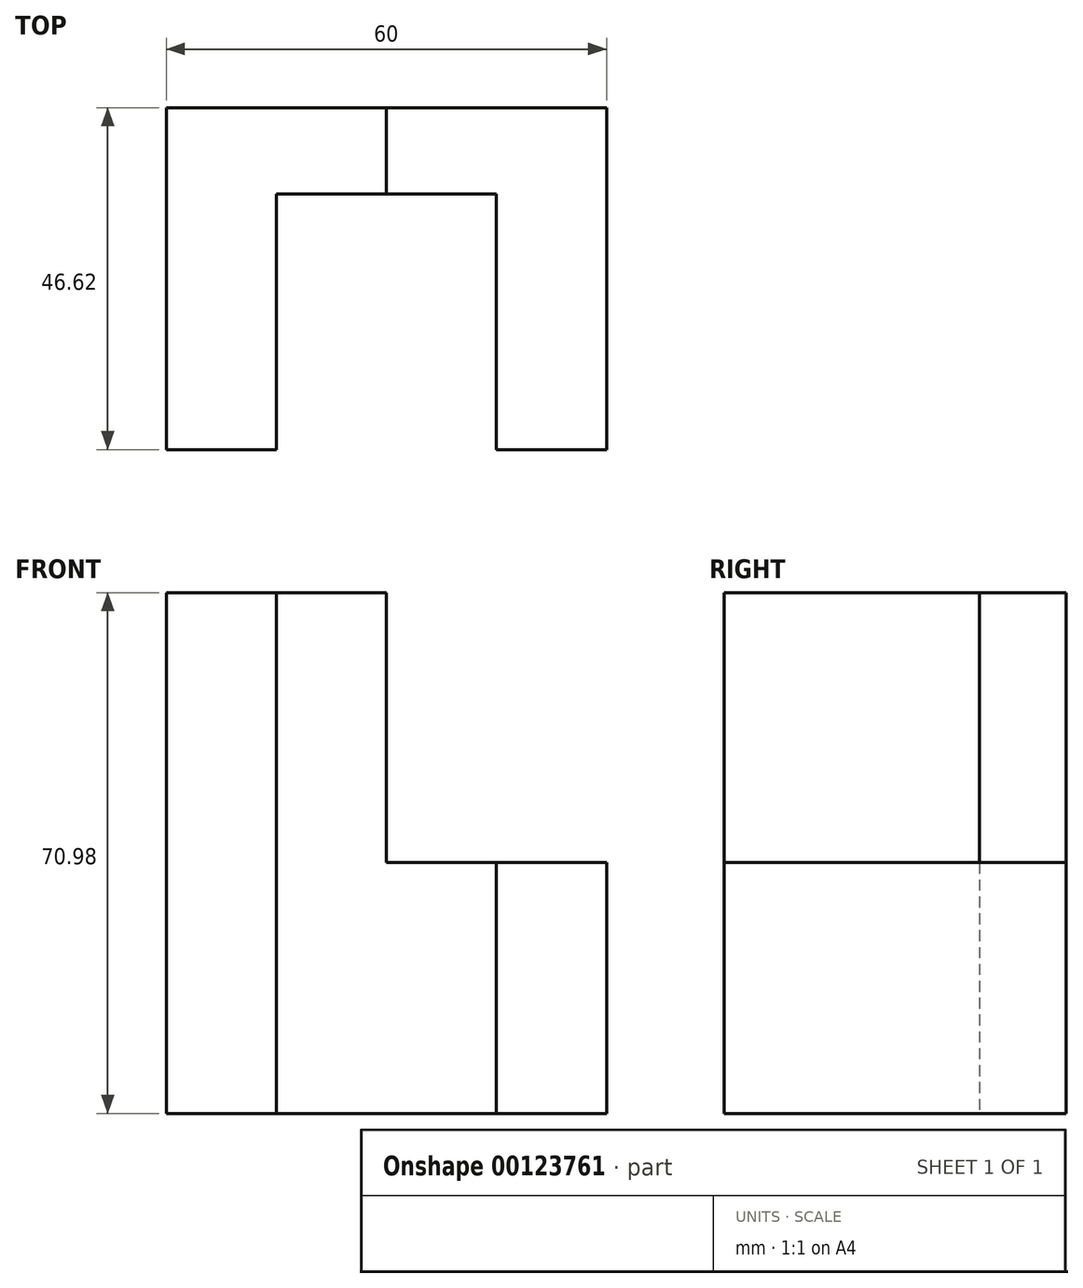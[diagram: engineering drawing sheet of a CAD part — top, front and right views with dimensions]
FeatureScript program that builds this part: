
annotation { "Feature Type Name" : "Feature", "Feature Type Description" : "" }
export const myFeature = defineFeature(function(context is Context, id is Id, definition is map)
    precondition{}
    {
        {
            var Q0;
            Q0=qCreatedBy(makeId("Top.planeOp"),FACE);
            var sketch = newSketch(context, id + "F0", { "sketchPlane" : qUnion([Q0])});
            skLineSegment(sketch, "E0", {"start": v(0, 0) * mm, "end": v(0, 46.62) * mm});
            skLineSegment(sketch, "E1", {"start": v(0, 46.62) * mm, "end": v(60, 46.62) * mm});
            skLineSegment(sketch, "E2", {"start": v(60, 46.62) * mm, "end": v(60, 0) * mm});
            skLineSegment(sketch, "E3", {"start": v(60, 0) * mm, "end": v(45, 0) * mm});
            skLineSegment(sketch, "E4", {"start": v(45, 0) * mm, "end": v(45, 34.85) * mm});
            skLineSegment(sketch, "E5", {"start": v(45, 34.85) * mm, "end": v(15, 34.85) * mm});
            skLineSegment(sketch, "E6", {"start": v(15, 34.85) * mm, "end": v(15, 0) * mm});
            skLineSegment(sketch, "E7", {"start": v(15, 0) * mm, "end": v(0, 0) * mm});
            skSolve(sketch);
        }
        {
            var Q0;
            Q0 = qSketchRegion(id + "F0", true);
            extrude(context, id + "F1", {"entities" : qUnion([Q0]), "depth" : 70.98 * mm});
        }
        {
            var Q0;
            Q0=qCreatedBy(makeId("Front.planeOp"),FACE);
            var sketch = newSketch(context, id + "F2", { "sketchPlane" : qUnion([Q0])});
            skLineSegment(sketch, "E8", {"start": v(60, 70.98) * mm, "end": v(60, 34.17) * mm});
            skLineSegment(sketch, "E9", {"start": v(60, 34.17) * mm, "end": v(30, 34.17) * mm});
            skLineSegment(sketch, "E10", {"start": v(30, 34.17) * mm, "end": v(30, 71.17) * mm});
            skLineSegment(sketch, "E11", {"start": v(30, 71.17) * mm, "end": v(60, 70.98) * mm});
            skSolve(sketch);
        }
        {
            var Q0;
            Q0 = qSketchRegion(id + "F2", true);
            extrude(context, id + "F3", {"entities" : qUnion([Q0]), "operationType" : NewBodyOperationType.REMOVE, "endBound" : BoundingType.THROUGH_ALL, "oppositeDirection" : true, "depth" : 25 * mm});
        }
    });
